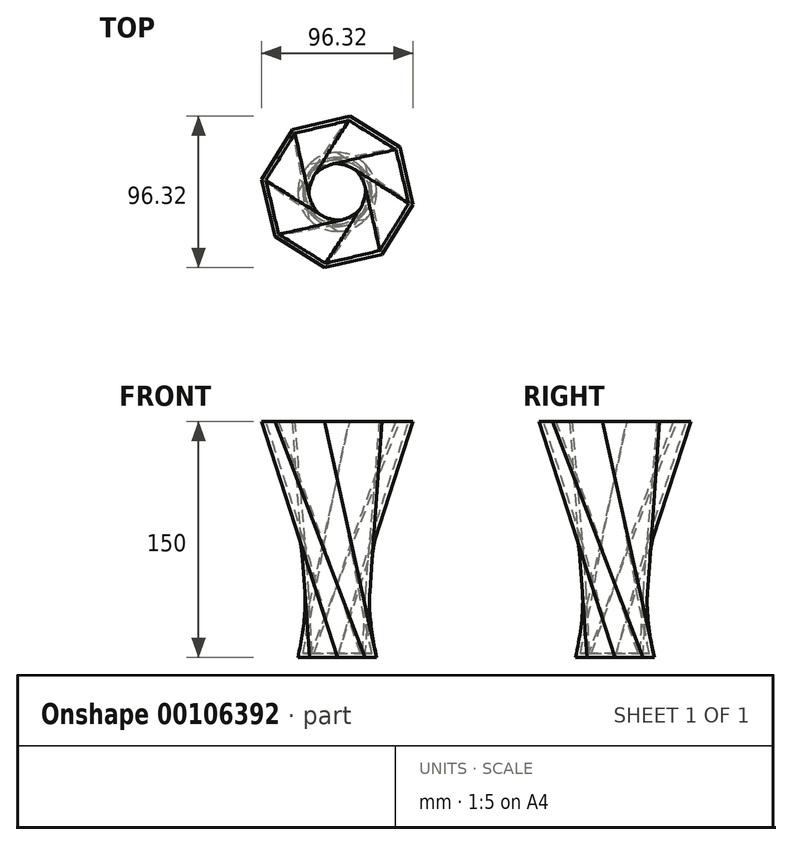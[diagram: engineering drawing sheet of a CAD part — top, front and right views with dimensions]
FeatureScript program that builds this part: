
annotation { "Feature Type Name" : "Feature", "Feature Type Description" : "" }
export const myFeature = defineFeature(function(context is Context, id is Id, definition is map)
    precondition{}
    {
        {
            var Q0;
            Q0=qCreatedBy(makeId("Top.planeOp"),FACE);
            var sketch = newSketch(context, id + "F0", { "sketchPlane" : qUnion([Q0])});
            skCircle(sketch, "E0", {"center": v(0, 0) * mm, "radius": 25 * mm});
            skPoint(sketch, "E1", {"position": v(-25, 0) * mm});
            skSolve(sketch);
        }
        {
            var Q0;
            Q0=qCreatedBy(makeId("Top.planeOp"),FACE);
            cPlane(context, id + "F1", {"entities" : qUnion([Q0]), "cplaneType" : CPlaneType.OFFSET, "offset" : 150 * mm, "width" : 150 * mm, "height" : 150 * mm});
        }
        {
            var Q0;
            Q0=qCreatedBy(id+"F1.planeOp",FACE);
            var sketch = newSketch(context, id + "F2", { "sketchPlane" : qUnion([Q0])});
            skCircle(sketch, "E2.cCircle", {"center": v(0, 0) * mm, "radius": 45.1 * mm, "construction": true});
            skLineSegment(sketch, "E2.0", {"start": v(-39.7, -28.41) * mm, "end": v(-48.16, 7.97) * mm});
            skLineSegment(sketch, "E2.1", {"start": v(-48.16, 7.97) * mm, "end": v(-28.41, 39.7) * mm});
            skLineSegment(sketch, "E2.2", {"start": v(-28.41, 39.7) * mm, "end": v(7.97, 48.16) * mm});
            skLineSegment(sketch, "E2.3", {"start": v(7.97, 48.16) * mm, "end": v(39.7, 28.41) * mm});
            skLineSegment(sketch, "E2.4", {"start": v(39.7, 28.41) * mm, "end": v(48.16, -7.97) * mm});
            skLineSegment(sketch, "E2.5", {"start": v(48.16, -7.97) * mm, "end": v(28.41, -39.7) * mm});
            skLineSegment(sketch, "E2.6", {"start": v(28.41, -39.7) * mm, "end": v(-7.97, -48.16) * mm});
            skLineSegment(sketch, "E2.7", {"start": v(-7.97, -48.16) * mm, "end": v(-39.7, -28.41) * mm});
            skPoint(sketch, "E2.0.midPoint", {"position": v(-43.92, -10.22) * mm});
            skSolve(sketch);
        }
        {
            var Q0;
            Q0=makeQuery(id+"F0.imprint","IMPRINT",FACE,{"disambiguationData":[TD([[makeQuery(id+"F0.imprint","IMPRINT",EDGE,{"derivedFrom":sQuery(id+"F0.wireOp",EDGE,"E0")}),1.0]])]});
            var Q1;
            Q1=makeQuery(id+"F2.imprint","IMPRINT",FACE,{"disambiguationData":[TD([[makeQuery(id+"F2.imprint","IMPRINT",EDGE,{"derivedFrom":sQuery(id+"F2.wireOp",EDGE,"E2.0")}),-1.0]])]});
            var Q2;
            Q2=sQuery(id+"F0.wireOp",VERTEX,"E1");
            var Q3;
            Q3=sQuery(id+"F2.wireOp",VERTEX,"E2.3.start");
            loft(context, id + "F3", {"sheetProfilesArray" : [{ "sheetProfileEntities" : qUnion([Q0]) }, { "sheetProfileEntities" : qUnion([Q1]) }], "matchConnections" : true, "connections" : [{ "connectionEntities" : qUnion([Q2, Q3]), "connectionEdgeQueries" : qUnion([]), "connectionEdgeParameters" : [] }]});
        }
        {
            var Q0;
            Q0=makeQuery(id+"F3.opLoft","CAP_FACE",FACE,{"disambiguationData":[OSD([makeQuery(id+"F2.imprint","IMPRINT",FACE,{"disambiguationData":[TD([[makeQuery(id+"F2.imprint","IMPRINT",EDGE,{"derivedFrom":sQuery(id+"F2.wireOp",EDGE,"E2.0")}),-1.0]])]})])],"isStart":true});
            shell(context, id + "F4", {"entities" : qUnion([Q0]), "thickness" : 2.5 * mm});
        }
    });
